# Revit family: SANINDUSA_108760004_Arc_46ArcUnderMountBasin›46_V0
name_source: partatom
category: Plumbing Fixtures
units: mm (PartAtom-declared; Revit-internal decimal feet)

## family parameters
Cut with Voids When Loaded = No
Host = Face
Part Type = Normal
Room Calculation Point = No
Round Connector Dimension = Use Diameter
Shared = No

## types (1)
- SANINDUSA_108760004_Arc_46ArcUnderMountBasin›46_V0
    AssetType = Fixed
    Category = Pr_40_20_96_18: Counter top wash basins
    CodePerformance = EN 14688:2006  CL 20
    Color = white
    Constituents = With embellisher ring
    Default Elevation = 1219 mm
    Description = Wastewater appliance for washing the upper parts of the body.
    DrainSize = 45 mm  [stored 0.147638 ft]
    Element Type = WASHHANDBASIN: Wastewater appliance for washing the upper parts of the body.
    Features = "Washbasin mounted on underside of countertop. Compatible
with Fixing kit 45, not included."
    Finish = gloss
    Installation Instructions = https://www.tec.sanindusa.pt
    Manufacturer = Sanindusa
    ManufacturerName = Sanindusa
    ManufacturerURL = www.tec.sanindusa.pt
    Material = vitreous china
    Model = 108760004
    ModelNumber = 108760004
    ModelReference = Arc
    Name = 46 Arc washbasin
    NominalDepth = 135 mm  [stored 0.442913 ft]
    NominalHeight = 185 mm  [stored 0.606955 ft]
    NominalLength = 460 mm  [stored 1.50919 ft]
    NominalWidth = 460 mm  [stored 1.50919 ft]
    Pre-defined type (IFC) = WASHHANDBASIN
    ProductInformation = https://www.tec.sanindusa.pt
    ProductionYear = 2003
    Shape = round
    Size = ø46
    SpilloverLevel = 95
    Type (IFC) = IfcSanitaryTerminalType
    URL = www.tec.sanindusa.pt
    Version = 1
    WarrantyDescription = https://www.tec.sanindusa.pt
    WarrantyDurationParts = 5
    WarrantyDurationUnit = year
    WashHandBasinMounting = other
    WashHandBasinType = handrinse
    Waste Connection = Yes
    Weight = 6.00 kg

note: [stored X ft] marks values corroborated as IEEE doubles in the binary element streams (Revit-internal decimal feet)

## geometry (parser evidence)
native form markers: Sweep x6
no freeform markers — native parametric forms only
